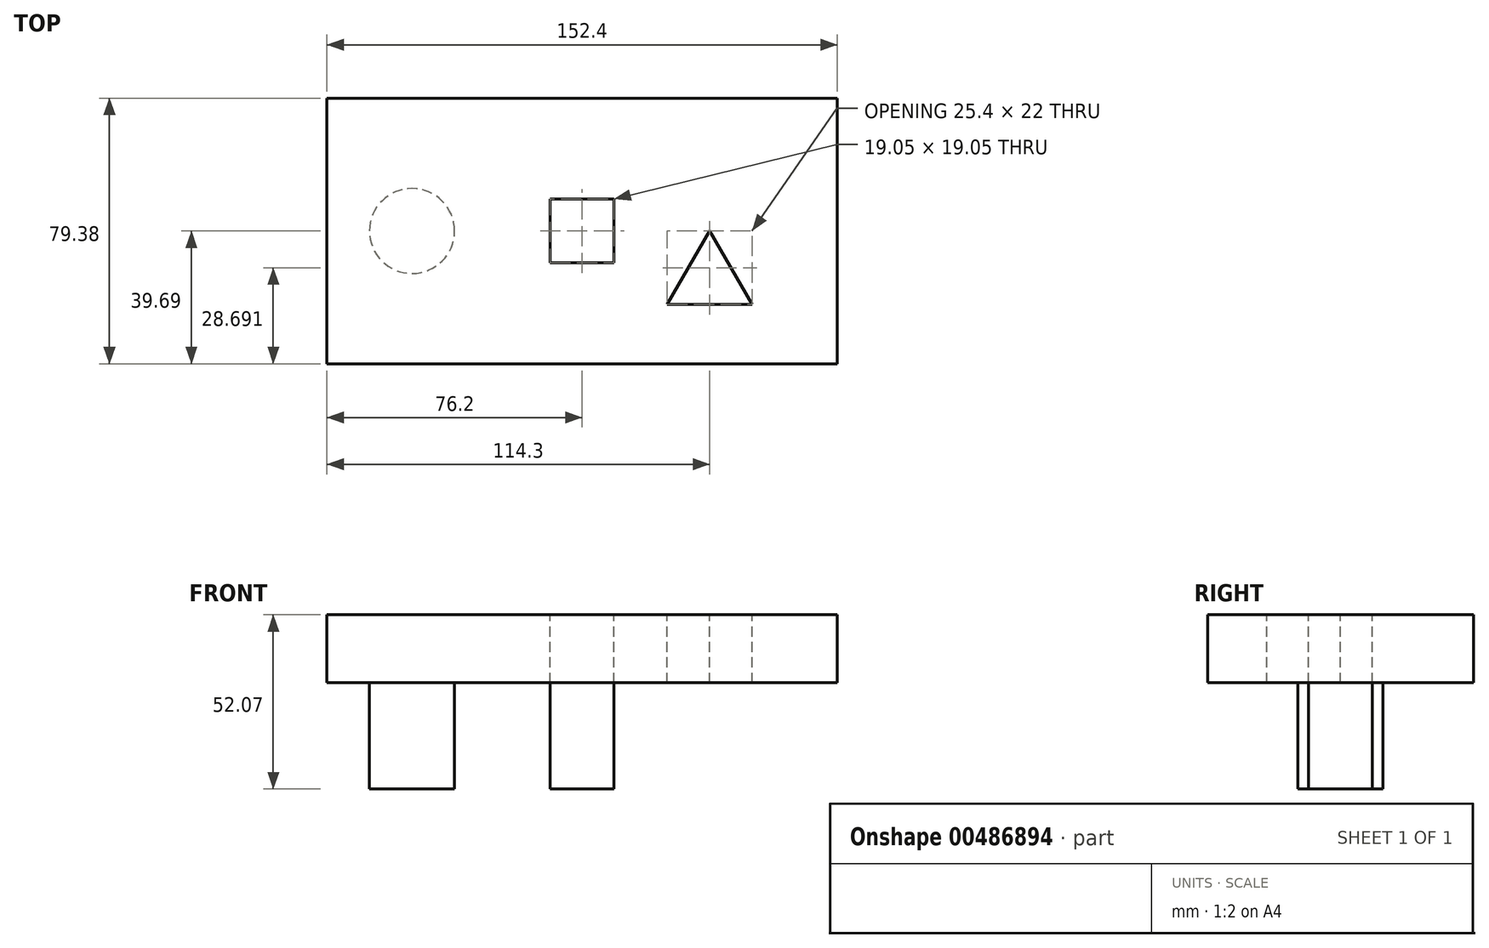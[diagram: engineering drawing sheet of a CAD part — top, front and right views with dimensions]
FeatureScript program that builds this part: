
annotation { "Feature Type Name" : "Feature", "Feature Type Description" : "" }
export const myFeature = defineFeature(function(context is Context, id is Id, definition is map)
    precondition{}
    {
        {
            var Q0;
            Q0=qCreatedBy(makeId("Top.planeOp"),FACE);
            var sketch = newSketch(context, id + "F0", { "sketchPlane" : qUnion([Q0])});
            skPoint(sketch, "E0", {"position": v(-31.75, 0) * mm});
            skLineSegment(sketch, "E1.bottom", {"start": v(44.45, 39.69) * mm, "end": v(-107.95, 39.69) * mm});
            skLineSegment(sketch, "E1.top", {"start": v(44.45, -39.69) * mm, "end": v(-107.95, -39.69) * mm});
            skLineSegment(sketch, "E1.left", {"start": v(44.45, 39.69) * mm, "end": v(44.45, -39.69) * mm});
            skLineSegment(sketch, "E1.right", {"start": v(-107.95, 39.69) * mm, "end": v(-107.95, -39.69) * mm});
            skPoint(sketch, "E2", {"position": v(0, -39.69) * mm});
            skSolve(sketch);
        }
        {
            var Q0;
            Q0=makeQuery(id+"F0.imprint","IMPRINT",FACE,{"disambiguationData":[TD([[makeQuery(id+"F0.imprint","IMPRINT",EDGE,{"derivedFrom":sQuery(id+"F0.wireOp",EDGE,"E1.bottom")}),1.0]])]});
            extrude(context, id + "F1", {"entities" : qUnion([Q0]), "depth" : 20.32 * mm});
        }
        {
            var Q0;
            Q0=makeQuery(id+"F1.opExtrude","CAP_FACE",FACE,{"disambiguationData":[OSD([sQuery(id+"F0.wireOp",EDGE,"E1.bottom"),sQuery(id+"F0.wireOp",EDGE,"E1.top"),sQuery(id+"F0.wireOp",EDGE,"E1.left"),sQuery(id+"F0.wireOp",EDGE,"E1.right")])],"isStart":false});
            var sketch = newSketch(context, id + "F2", { "sketchPlane" : qUnion([Q0])});
            skPoint(sketch, "E3", {"position": v(-31.75, 0) * mm});
            skLineSegment(sketch, "E4.bottom", {"start": v(-22.22, 9.52) * mm, "end": v(-41.27, 9.52) * mm});
            skLineSegment(sketch, "E4.top", {"start": v(-22.22, -9.53) * mm, "end": v(-41.27, -9.53) * mm});
            skLineSegment(sketch, "E4.left", {"start": v(-22.22, 9.52) * mm, "end": v(-22.22, -9.53) * mm});
            skLineSegment(sketch, "E4.right", {"start": v(-41.27, 9.52) * mm, "end": v(-41.27, -9.53) * mm});
            skSolve(sketch);
        }
        {
            var Q0;
            Q0=makeQuery(id+"F2.imprint","IMPRINT",FACE,{"disambiguationData":[TD([[makeQuery(id+"F2.imprint","IMPRINT",EDGE,{"derivedFrom":sQuery(id+"F2.wireOp",EDGE,"E4.bottom")}),1.0]])]});
            extrude(context, id + "F3", {"entities" : qUnion([Q0]), "operationType" : NewBodyOperationType.ADD, "oppositeDirection" : true, "depth" : 52.07 * mm});
        }
        {
            var Q0;
            Q0=makeQuery(id+"F2.imprint","IMPRINT",FACE,{"disambiguationData":[TD([[makeQuery(id+"F2.imprint","IMPRINT",EDGE,{"derivedFrom":sQuery(id+"F2.wireOp",EDGE,"E4.bottom")}),1.0]])]});
            extrude(context, id + "F4", {"entities" : qUnion([Q0]), "operationType" : NewBodyOperationType.REMOVE, "oppositeDirection" : true, "depth" : 20.32 * mm});
        }
        {
            var Q0;
            Q0=makeQuery(id+"F2.imprint","IMPRINT",FACE,{"disambiguationData":[TD([[makeQuery(id+"F2.imprint","IMPRINT",EDGE,{"derivedFrom":sQuery(id+"F2.wireOp",EDGE,"E4.bottom")}),-1.0]])]});
            var sketch = newSketch(context, id + "F5", { "sketchPlane" : qUnion([Q0])});
            skPoint(sketch, "E5", {"position": v(-82.55, 0) * mm});
            skCircle(sketch, "E6", {"center": v(-82.55, 0) * mm, "radius": 12.7 * mm});
            skSolve(sketch);
        }
        {
            var Q0;
            Q0=makeQuery(id+"F5.imprint","IMPRINT",FACE,{"disambiguationData":[TD([[makeQuery(id+"F5.imprint","IMPRINT",EDGE,{"derivedFrom":sQuery(id+"F5.wireOp",EDGE,"E6")}),1.0]])]});
            extrude(context, id + "F6", {"entities" : qUnion([Q0]), "operationType" : NewBodyOperationType.ADD, "oppositeDirection" : true, "depth" : 52.07 * mm});
        }
        {
            var Q0;
            Q0=makeQuery(id+"F1.opExtrude","CAP_FACE",FACE,{"disambiguationData":[OSD([sQuery(id+"F0.wireOp",EDGE,"E1.bottom"),sQuery(id+"F0.wireOp",EDGE,"E1.top"),sQuery(id+"F0.wireOp",EDGE,"E1.left"),sQuery(id+"F0.wireOp",EDGE,"E1.right")])],"isStart":false});
            var sketch = newSketch(context, id + "F7", { "sketchPlane" : qUnion([Q0])});
            skPoint(sketch, "E7", {"position": v(6.35, 0) * mm});
            skLineSegment(sketch, "E8", {"start": v(6.35, 0) * mm, "end": v(-6.35, -22) * mm});
            skLineSegment(sketch, "E9", {"start": v(-6.35, -22) * mm, "end": v(19.05, -22) * mm});
            skLineSegment(sketch, "E10", {"start": v(19.05, -22) * mm, "end": v(6.35, 0) * mm});
            skSolve(sketch);
        }
        {
            var Q0;
            Q0=makeQuery(id+"F7.imprint","IMPRINT",FACE,{"disambiguationData":[TD([[makeQuery(id+"F7.imprint","IMPRINT",EDGE,{"derivedFrom":sQuery(id+"F7.wireOp",EDGE,"E8")}),1.0]])]});
            extrude(context, id + "F8", {"entities" : qUnion([Q0]), "operationType" : NewBodyOperationType.REMOVE, "oppositeDirection" : true, "depth" : 20.32 * mm});
        }
    });
